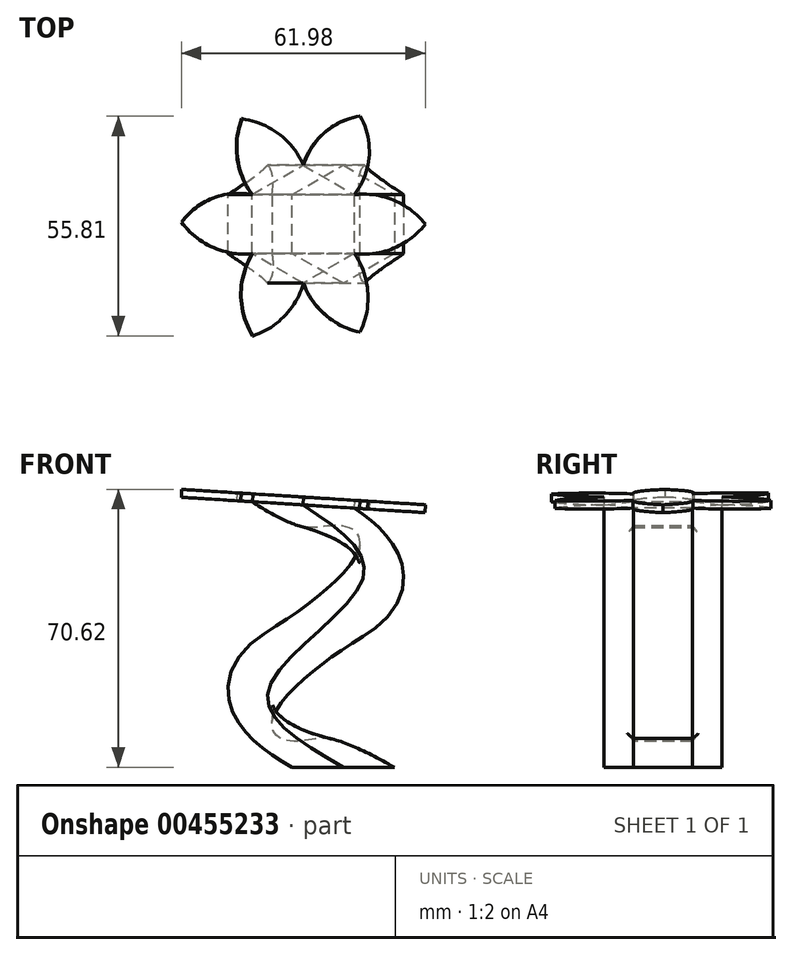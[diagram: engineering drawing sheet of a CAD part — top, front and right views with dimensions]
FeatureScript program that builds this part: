
annotation { "Feature Type Name" : "Feature", "Feature Type Description" : "" }
export const myFeature = defineFeature(function(context is Context, id is Id, definition is map)
    precondition{}
    {
        {
            var Q0;
            Q0=qCreatedBy(makeId("Top.planeOp"),FACE);
            var sketch = newSketch(context, id + "F0", { "sketchPlane" : qUnion([Q0])});
            skCircle(sketch, "E0.cCircle", {"center": v(0, 0) * mm, "radius": 13 * mm, "construction": true});
            skLineSegment(sketch, "E0.0", {"start": v(-13, 7.5) * mm, "end": v(0, 15) * mm});
            skLineSegment(sketch, "E0.1", {"start": v(0, 15) * mm, "end": v(13, 7.5) * mm});
            skLineSegment(sketch, "E0.2", {"start": v(13, 7.5) * mm, "end": v(13, -7.5) * mm});
            skLineSegment(sketch, "E0.3", {"start": v(13, -7.5) * mm, "end": v(0, -15) * mm});
            skLineSegment(sketch, "E0.4", {"start": v(0, -15) * mm, "end": v(-13, -7.5) * mm});
            skLineSegment(sketch, "E0.5", {"start": v(-13, -7.5) * mm, "end": v(-13, 7.5) * mm});
            skPoint(sketch, "E0.0.midPoint", {"position": v(-6.5, 11.25) * mm});
            skSolve(sketch);
        }
        {
            var Q0;
            Q0=qCreatedBy(makeId("Front.planeOp"),FACE);
            var sketch = newSketch(context, id + "F1", { "sketchPlane" : qUnion([Q0])});
            skFitSpline(sketch, "E1", {"points": [v(0, 0) * mm, v(-18.99, 19.67) * mm, v(5.03, 48.03) * mm, v(-10.22, 66.67) * mm], "startDerivative": vector(-97.5, 56.51) * mm, "endDerivative": vector(-86, 57.38) * mm});
            skSolve(sketch);
        }
        {
            var Q0;
            Q0=makeQuery(id+"F0.imprint","IMPRINT",FACE,{"disambiguationData":[TD([[makeQuery(id+"F0.imprint","IMPRINT",EDGE,{"derivedFrom":sQuery(id+"F0.wireOp",EDGE,"E0.0")}),-1.0]])]});
            var Q1;
            Q1=sQuery(id+"F1.wireOp",EDGE,"E1");
            sweep(context, id + "F2", {"profiles" : qUnion([Q0]), "path" : qUnion([Q1])});
        }
        {
            var Q0;
            Q0=makeQuery(id+"F2.opSweep","CAP_FACE",FACE,{"disambiguationData":[OSD([sQuery(id+"F0.wireOp",EDGE,"E0.0"),sQuery(id+"F0.wireOp",EDGE,"E0.1"),sQuery(id+"F0.wireOp",EDGE,"E0.2"),sQuery(id+"F0.wireOp",EDGE,"E0.3"),sQuery(id+"F0.wireOp",EDGE,"E0.4"),sQuery(id+"F0.wireOp",EDGE,"E0.5"),sQuery(id+"F1.wireOp",VERTEX,"E1.end")])],"isStart":false});
            var sketch = newSketch(context, id + "F3", { "sketchPlane" : qUnion([Q0])});
            skPoint(sketch, "E2.0.midPoint", {"position": v(-27.27, -0.18) * mm});
            skCircle(sketch, "E3", {"center": v(-14.4, 0) * mm, "radius": 13 * mm});
            skArc(sketch, "E4", {"start": v(16.58, 0) * mm, "mid": v(8.56, 6.1) * mm, "end": v(-1.42, 7.5) * mm});
            skArc(sketch, "E5", {"start": v(-1.42, -7.5) * mm, "mid": v(8.56, -6.1) * mm, "end": v(16.58, 0) * mm});
            skArc(sketch, "E6", {"start": v(0, -27.44) * mm, "mid": v(1.96, -17.28) * mm, "end": v(-1.42, -7.5) * mm});
            skArc(sketch, "E7", {"start": v(-14.4, -15) * mm, "mid": v(-8.78, -23.04) * mm, "end": v(0, -27.44) * mm});
            skArc(sketch, "E8", {"start": v(-45.4, 0.49) * mm, "mid": v(-37.45, -5.87) * mm, "end": v(-27.4, -7.5) * mm});
            skArc(sketch, "E9", {"start": v(-27.4, 7.5) * mm, "mid": v(-37.42, 6.61) * mm, "end": v(-45.4, 0.49) * mm});
            skArc(sketch, "E10", {"start": v(-1.42, 7.5) * mm, "mid": v(2.31, 17.25) * mm, "end": v(0, 27.44) * mm});
            skArc(sketch, "E11", {"start": v(0, 27.44) * mm, "mid": v(-8.98, 23.28) * mm, "end": v(-14.4, 15) * mm});
            skArc(sketch, "E12", {"start": v(-14.4, 15) * mm, "mid": v(-20.67, 22.92) * mm, "end": v(-30.01, 26.77) * mm});
            skArc(sketch, "E13", {"start": v(-30.01, 26.77) * mm, "mid": v(-31.2, 16.8) * mm, "end": v(-27.4, 7.5) * mm});
            skLineSegment(sketch, "E14", {"start": v(-1.42, 7.5) * mm, "end": v(-1.42, -7.5) * mm});
            skArc(sketch, "E15", {"start": v(-27.24, -28.37) * mm, "mid": v(-19.18, -23.26) * mm, "end": v(-14.4, -15) * mm});
            skArc(sketch, "E16", {"start": v(-27.4, -7.5) * mm, "mid": v(-30.26, -17.96) * mm, "end": v(-27.24, -28.37) * mm});
            skSolve(sketch);
        }
        {
            var Q0;
            Q0=makeQuery(id+"F2.opSweep","CAP_FACE",FACE,{"disambiguationData":[OSD([sQuery(id+"F0.wireOp",EDGE,"E0.0"),sQuery(id+"F0.wireOp",EDGE,"E0.1"),sQuery(id+"F0.wireOp",EDGE,"E0.2"),sQuery(id+"F0.wireOp",EDGE,"E0.3"),sQuery(id+"F0.wireOp",EDGE,"E0.4"),sQuery(id+"F0.wireOp",EDGE,"E0.5"),sQuery(id+"F1.wireOp",VERTEX,"E1.end")])],"isStart":false});
            var sketch = newSketch(context, id + "F4", { "sketchPlane" : qUnion([Q0])});
            skLineSegment(sketch, "E17", {"start": v(-14.4, -15) * mm, "end": v(-27.4, -7.5) * mm});
            skLineSegment(sketch, "E18", {"start": v(-27.4, -7.5) * mm, "end": v(-27.4, 7.5) * mm});
            skLineSegment(sketch, "E19", {"start": v(-27.4, 7.5) * mm, "end": v(-14.4, 15) * mm});
            skLineSegment(sketch, "E20", {"start": v(-14.4, 15) * mm, "end": v(-1.42, 7.5) * mm});
            skLineSegment(sketch, "E21", {"start": v(-1.42, 7.5) * mm, "end": v(-1.42, -7.5) * mm});
            skLineSegment(sketch, "E22", {"start": v(-1.42, -7.5) * mm, "end": v(-14.4, -15) * mm});
            skSolve(sketch);
        }
        {
            var Q0;
            Q0=makeQuery(id+"F4.imprint","IMPRINT",FACE,{"disambiguationData":[TD([[makeQuery(id+"F4.imprint","IMPRINT",EDGE,{"derivedFrom":sQuery(id+"F4.wireOp",EDGE,"E17")}),1.0]])]});
            extrude(context, id + "F5", {"entities" : qUnion([Q0]), "operationType" : NewBodyOperationType.ADD, "depth" : 2 * mm, "offsetDistance" : 25 * mm});
        }
        {
            var Q0;
            {var subQ0=sQuery(id+"F3.wireOp",EDGE,"E8");Q0=makeQuery(id+"F3.imprint","IMPRINT",FACE,{"disambiguationData":[TD([[makeQuery(id+"F3.imprint","IMPRINT",EDGE,{"derivedFrom":subQ0}),1.0]])]});}
            var Q1;
            {var subQ0=sQuery(id+"F3.wireOp",EDGE,"E12");Q1=makeQuery(id+"F3.imprint","IMPRINT",FACE,{"disambiguationData":[TD([[makeQuery(id+"F3.imprint","IMPRINT",EDGE,{"derivedFrom":subQ0}),1.0]])]});}
            var Q2;
            {var subQ0=sQuery(id+"F3.wireOp",EDGE,"E10");Q2=makeQuery(id+"F3.imprint","IMPRINT",FACE,{"disambiguationData":[TD([[makeQuery(id+"F3.imprint","IMPRINT",EDGE,{"derivedFrom":subQ0}),1.0]])]});}
            var Q3;
            {var subQ0=sQuery(id+"F3.wireOp",EDGE,"E4");Q3=makeQuery(id+"F3.imprint","IMPRINT",FACE,{"disambiguationData":[TD([[makeQuery(id+"F3.imprint","IMPRINT",EDGE,{"derivedFrom":subQ0}),1.0]])]});}
            var Q4;
            {var subQ0=sQuery(id+"F3.wireOp",EDGE,"E6");Q4=makeQuery(id+"F3.imprint","IMPRINT",FACE,{"disambiguationData":[TD([[makeQuery(id+"F3.imprint","IMPRINT",EDGE,{"derivedFrom":subQ0}),1.0]])]});}
            var Q5;
            {var subQ0=sQuery(id+"F3.wireOp",EDGE,"E15");Q5=makeQuery(id+"F3.imprint","IMPRINT",FACE,{"disambiguationData":[TD([[makeQuery(id+"F3.imprint","IMPRINT",EDGE,{"derivedFrom":subQ0}),1.0]])]});}
            extrude(context, id + "F6", {"entities" : qUnion([Q0, Q1, Q2, Q3, Q4, Q5]), "operationType" : NewBodyOperationType.ADD, "depth" : 2 * mm, "offsetDistance" : 25 * mm});
        }
    });
